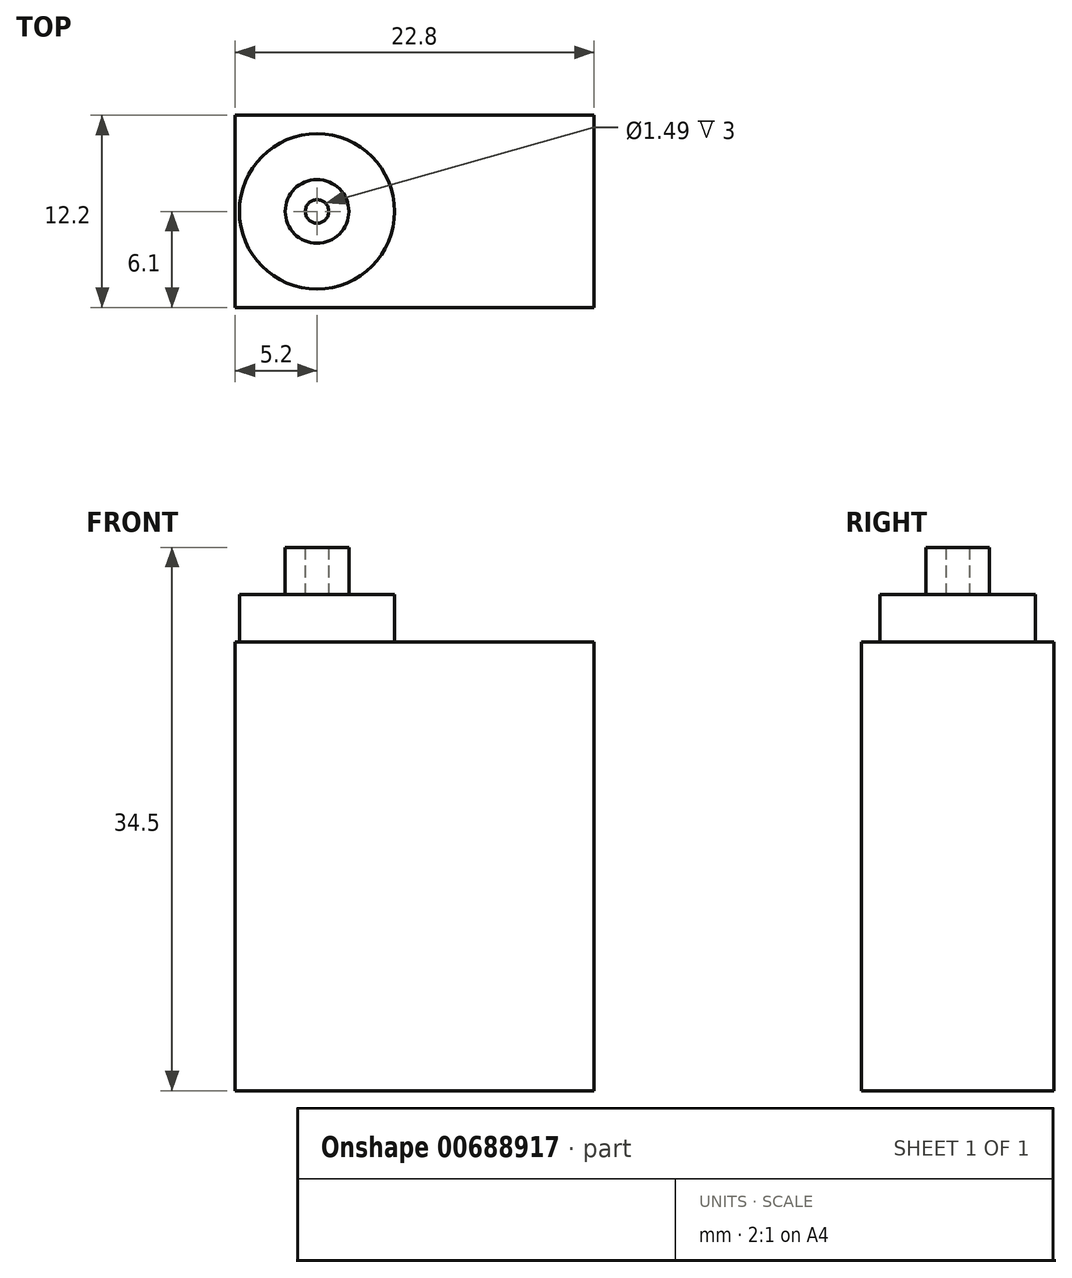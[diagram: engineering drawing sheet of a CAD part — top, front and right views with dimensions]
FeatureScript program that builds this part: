
annotation { "Feature Type Name" : "Feature", "Feature Type Description" : "" }
export const myFeature = defineFeature(function(context is Context, id is Id, definition is map)
    precondition{}
    {
        {
            var Q0;
            Q0=qCreatedBy(makeId("Front.planeOp"),FACE);
            var sketch = newSketch(context, id + "F0", { "sketchPlane" : qUnion([Q0])});
            skLineSegment(sketch, "E0.bottom", {"start": v(0, 0) * mm, "end": v(22.8, 0) * mm});
            skLineSegment(sketch, "E0.top", {"start": v(0, 28.5) * mm, "end": v(22.8, 28.5) * mm});
            skLineSegment(sketch, "E0.left", {"start": v(0, 0) * mm, "end": v(0, 28.5) * mm});
            skLineSegment(sketch, "E0.right", {"start": v(22.8, 0) * mm, "end": v(22.8, 28.5) * mm});
            skSolve(sketch);
        }
        {
            var Q0;
            Q0=makeQuery(id+"F0.imprint","IMPRINT",FACE,{"disambiguationData":[TD([[makeQuery(id+"F0.imprint","IMPRINT",EDGE,{"derivedFrom":sQuery(id+"F0.wireOp",EDGE,"E0.bottom")}),1.0]])]});
            extrude(context, id + "F1", {"entities" : qUnion([Q0]), "depth" : 12.2 * mm, "offsetDistance" : 25 * mm});
        }
        {
            var Q0;
            Q0=makeQuery(id+"F1.opExtrude","SWEPT_FACE",FACE,{"disambiguationData":[OSD([sQuery(id+"F0.wireOp",EDGE,"E0.top")])]});
            var sketch = newSketch(context, id + "F2", { "sketchPlane" : qUnion([Q0])});
            skCircle(sketch, "E1", {"center": v(5.2, -6.1) * mm, "radius": 4.93 * mm});
            skPoint(sketch, "E1.centerSnap0", {"position": v(0, -6.1) * mm});
            skSolve(sketch);
        }
        {
            var Q0;
            Q0 = qSketchRegion(id + "F2", true);
            extrude(context, id + "F3", {"entities" : qUnion([Q0]), "operationType" : NewBodyOperationType.ADD, "depth" : 3 * mm, "offsetDistance" : 25 * mm});
        }
        {
            var Q0;
            Q0=makeQuery(id+"F3.opExtrude","CAP_FACE",FACE,{"disambiguationData":[OSD([sQuery(id+"F2.wireOp",EDGE,"E1")])],"isStart":false});
            var sketch = newSketch(context, id + "F4", { "sketchPlane" : qUnion([Q0])});
            skCircle(sketch, "E2", {"center": v(5.2, -6.1) * mm, "radius": 2.02 * mm});
            skCircle(sketch, "E3", {"center": v(5.2, -6.1) * mm, "radius": 0.74 * mm});
            skSolve(sketch);
        }
        {
            var Q0;
            Q0=makeQuery(id+"F4.imprint","IMPRINT",FACE,{"disambiguationData":[TD([[makeQuery(id+"F4.imprint","IMPRINT",EDGE,{"derivedFrom":sQuery(id+"F4.wireOp",EDGE,"E2")}),1.0]])]});
            extrude(context, id + "F5", {"entities" : qUnion([Q0]), "operationType" : NewBodyOperationType.ADD, "depth" : 3 * mm, "offsetDistance" : 25 * mm});
        }
    });
